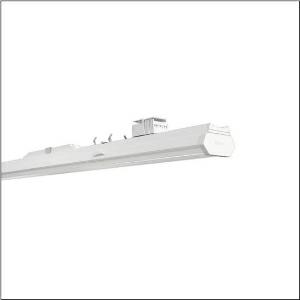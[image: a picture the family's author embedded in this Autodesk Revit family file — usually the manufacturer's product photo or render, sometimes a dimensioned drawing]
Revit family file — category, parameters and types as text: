
# Revit family: licross_11_protected_mo_51tp12dn495g
name_source: partatom
category: Lighting Fixtures
units: mm (PartAtom-declared; Revit-internal decimal feet)

## family parameters
Cut with Voids When Loaded = No
Host = Face
Light Source = No
Part Type = Normal
Room Calculation Point = No
Round Connector Dimension = Use Diameter
Shared = No

## types (1)
- --- (1 x LED, 9980 lm, 57.1 W, 4000K)
    Apparent Load = 57 VA
    CIE Flux Codes = 73 92 98 99 100
    Color Rendering = 80
    Color Temperature = 4000K
    Default Elevation = 1800 mm
    Description = Licross 11 Protected MO, luminaire insert, of sheet steel, galvanised, coil coated, white, length: 1.500mm, width: 90mm, height: 101mm, LED rated luminous flux: 9.980lm, light colour: 840, SDCM (Standard Deviation of Colour Matching)MacAdam ≤ 2 SDCM (initial), control gear: DALI 2, with plug, 5-pole, with phase selection, mains connection: 220..240V, AC, 50/60Hz, rated input power: 57W, internal wiring halogen-free, primary optical cover: cover, of PMMA, light emission: direct distribution, primary light characteristic: symmetric, protection rating (complete): IP64, insulation class (complete): insulation class I (protective earthing), certification: CE, ENEC, VDE, UKCA, protection symbol: D if used in an environment with conductive dust loads with corresponding accessories, impact resistance: IK06, permissible ambient temperature for indoor applications: -25..+35°C, corresponds to IFS (International Featured Standards) requirements for safety and quality in the food industry, reducing of maximum allowable ambient temperature of 5°C with ceiling mounting, LABS conformity tested according to VDMA 24364:2018-05, The light source and the operating device comply with the requirements of the Ecodesign Regulation (EU) 2019/2020 and are replaceable in accordance with this regulation, packaging unit: 1 piece
    Height = 92 mm
    Lamp = 1 x LED
    Lamp Light Flux = 9980 lm
    Lamp Power = 57.1 W
    Lamp count = 1
    Length = 1500 mm
    Luminous efficacy = 175 lm/W
    Manufacturer = Siteco
    ModVariant = No
    Model = 51TP12DN495G
    Mounting Place = Ceiling
    Mounting Type = Pendant
    Number of Poles = 1
    OnlyDefault = Yes
    Power Factor = 1
    Product Name = Licross 11 Protected MO
    Product group = luminaire insert | ceiling pendant
    ProductGroupID = 901
    Protection Class = Protection class I
    Protection Degree = IP 64
    RLX_Detail_Level = 1
    RLX_Emergency_Light_Flux = 0 lm
    RLX_Emergency_Type = 0
    RLX_Emergency_Type_DB = No
    RlxData = <blob elided: 24753 chars, md5=4297b0db>
    Socket = socket
    Standby Power = 0 W
    System Light Flux = 9980 lm
    System Power = 57 W
    Type Comments = factory setting: luminous flux: 100 % | dim-lin: 254 | 378 mA
    Type Image = l_1256148.jpg
    URL = http://relux.com
    VarID = @adj_102683
    Voltage = 0 V
    Weight = 0.00 kg
    Width = 88 mm

## geometry (parser evidence)
native form markers: Blend x4, Sweep x8
no freeform markers — native parametric forms only
